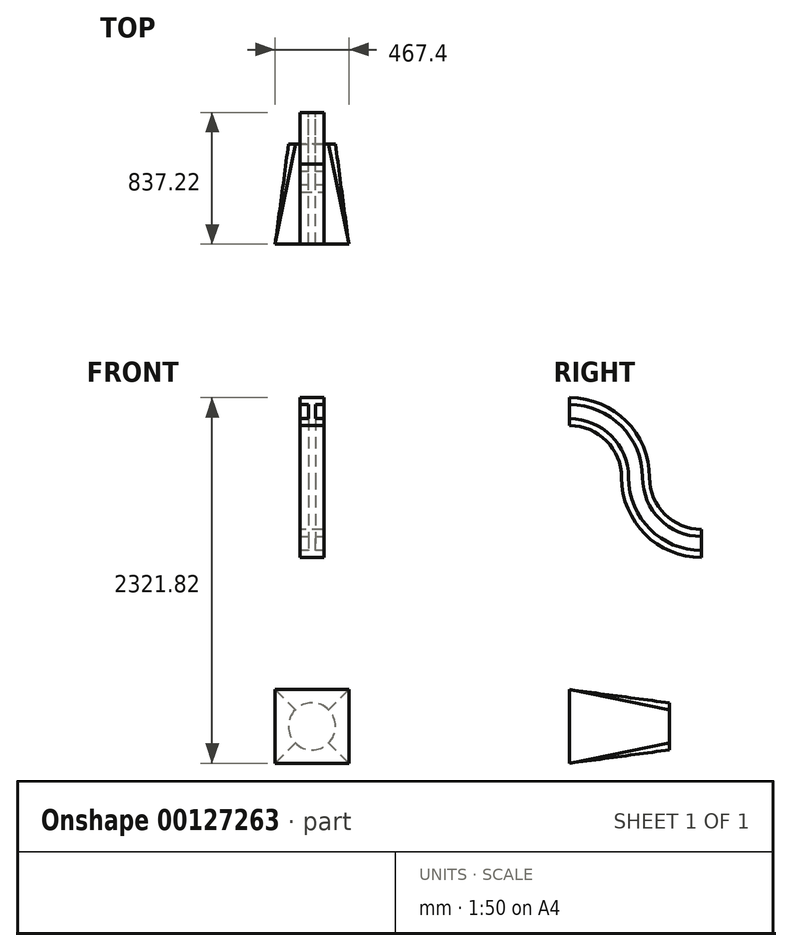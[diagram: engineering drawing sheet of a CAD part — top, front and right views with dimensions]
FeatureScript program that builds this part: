
annotation { "Feature Type Name" : "Feature", "Feature Type Description" : "" }
export const myFeature = defineFeature(function(context is Context, id is Id, definition is map)
    precondition{}
    {
        {
            var Q0;
            Q0=qCreatedBy(makeId("Front.planeOp"),FACE);
            var sketch = newSketch(context, id + "F0", { "sketchPlane" : qUnion([Q0])});
            skLineSegment(sketch, "E0", {"start": v(-76.2, 88.9) * mm, "end": v(-76.2, 44.45) * mm});
            skLineSegment(sketch, "E1", {"start": v(-76.2, 44.45) * mm, "end": v(-22.22, 44.45) * mm});
            skLineSegment(sketch, "E2", {"start": v(-22.23, 44.45) * mm, "end": v(-22.22, -44.45) * mm});
            skLineSegment(sketch, "E3", {"start": v(-22.22, -44.45) * mm, "end": v(-76.2, -44.45) * mm});
            skLineSegment(sketch, "E4", {"start": v(-76.2, -44.45) * mm, "end": v(-76.2, -88.9) * mm});
            skLineSegment(sketch, "E5", {"start": v(-76.2, -88.9) * mm, "end": v(76.2, -88.9) * mm});
            skLineSegment(sketch, "E6", {"start": v(76.2, -88.9) * mm, "end": v(76.2, -44.45) * mm});
            skLineSegment(sketch, "E7", {"start": v(76.2, -44.45) * mm, "end": v(22.22, -44.45) * mm});
            skLineSegment(sketch, "E8", {"start": v(22.22, -44.45) * mm, "end": v(22.22, 44.45) * mm});
            skLineSegment(sketch, "E9", {"start": v(22.22, 44.45) * mm, "end": v(76.2, 44.45) * mm});
            skLineSegment(sketch, "E10", {"start": v(76.2, 44.45) * mm, "end": v(76.2, 88.9) * mm});
            skLineSegment(sketch, "E11", {"start": v(76.2, 88.9) * mm, "end": v(-76.2, 88.9) * mm});
            skLineSegment(sketch, "E12", {"start": v(0, 88.9) * mm, "end": v(0, -88.9) * mm, "construction": true});
            skLineSegment(sketch, "E13", {"start": v(-22.22, 0) * mm, "end": v(22.22, 0) * mm, "construction": true});
            skSolve(sketch);
        }
        {
            var Q0;
            Q0=qCreatedBy(makeId("Right.planeOp"),FACE);
            var sketch = newSketch(context, id + "F1", { "sketchPlane" : qUnion([Q0])});
            skArc(sketch, "E14", {"start": v(418.61, -418.61) * mm, "mid": v(296, -122.6) * mm, "end": v(0, 0) * mm});
            skArc(sketch, "E15", {"start": v(418.61, -418.61) * mm, "mid": v(541.22, -714.61) * mm, "end": v(837.22, -837.22) * mm});
            skPoint(sketch, "E15.endSnap0", {"position": v(0, -837.22) * mm});
            skSolve(sketch);
        }
        {
            var Q0;
            Q0=makeQuery(id+"F0.imprint","IMPRINT",FACE,{"disambiguationData":[TD([[makeQuery(id+"F0.imprint","IMPRINT",EDGE,{"derivedFrom":sQuery(id+"F0.wireOp",EDGE,"E0")}),1.0]])]});
            var Q1;
            Q1=qConstructionFilter(qBodyType(qCreatedBy(id+"F1",EDGE),BodyType.WIRE),ConstructionObject.NO);
            sweep(context, id + "F2", {"profiles" : qUnion([Q0]), "path" : qUnion([Q1])});
        }
        {
            var Q0;
            Q0=qCreatedBy(makeId("Front.planeOp"),FACE);
            var sketch = newSketch(context, id + "F3", { "sketchPlane" : qUnion([Q0])});
            skLineSegment(sketch, "E16.bottom", {"start": v(-233.7, -1765.52) * mm, "end": v(233.7, -1765.52) * mm});
            skLineSegment(sketch, "E16.top", {"start": v(-233.7, -2232.92) * mm, "end": v(233.7, -2232.92) * mm});
            skLineSegment(sketch, "E16.left", {"start": v(-233.7, -1765.52) * mm, "end": v(-233.7, -2232.92) * mm});
            skLineSegment(sketch, "E16.right", {"start": v(233.7, -1765.52) * mm, "end": v(233.7, -2232.92) * mm});
            skSolve(sketch);
        }
        {
            var Q0;
            Q0=qCreatedBy(makeId("Front.planeOp"),FACE);
            cPlane(context, id + "F4", {"entities" : qUnion([Q0]), "cplaneType" : CPlaneType.OFFSET, "offset" : 635 * mm, "oppositeDirection" : true, "width" : 152.4 * mm, "height" : 152.4 * mm});
        }
        {
            var Q0;
            Q0=qCreatedBy(id+"F4.planeOp",FACE);
            var sketch = newSketch(context, id + "F5", { "sketchPlane" : qUnion([Q0])});
            skCircle(sketch, "E17", {"center": v(0, -1999.22) * mm, "radius": 149.22 * mm});
            skSolve(sketch);
        }
        {
            var Q0;
            Q0=makeQuery(id+"F3.imprint","IMPRINT",FACE,{"disambiguationData":[TD([[makeQuery(id+"F3.imprint","IMPRINT",EDGE,{"derivedFrom":sQuery(id+"F3.wireOp",EDGE,"E16.bottom")}),-1.0]])]});
            var Q1;
            Q1=makeQuery(id+"F5.imprint","IMPRINT",FACE,{"disambiguationData":[TD([[makeQuery(id+"F5.imprint","IMPRINT",EDGE,{"derivedFrom":sQuery(id+"F5.wireOp",EDGE,"E17")}),1.0]])]});
            loft(context, id + "F6", {"sheetProfilesArray" : [{ "sheetProfileEntities" : qUnion([Q0]) }, { "sheetProfileEntities" : qUnion([Q1]) }]});
        }
    });
